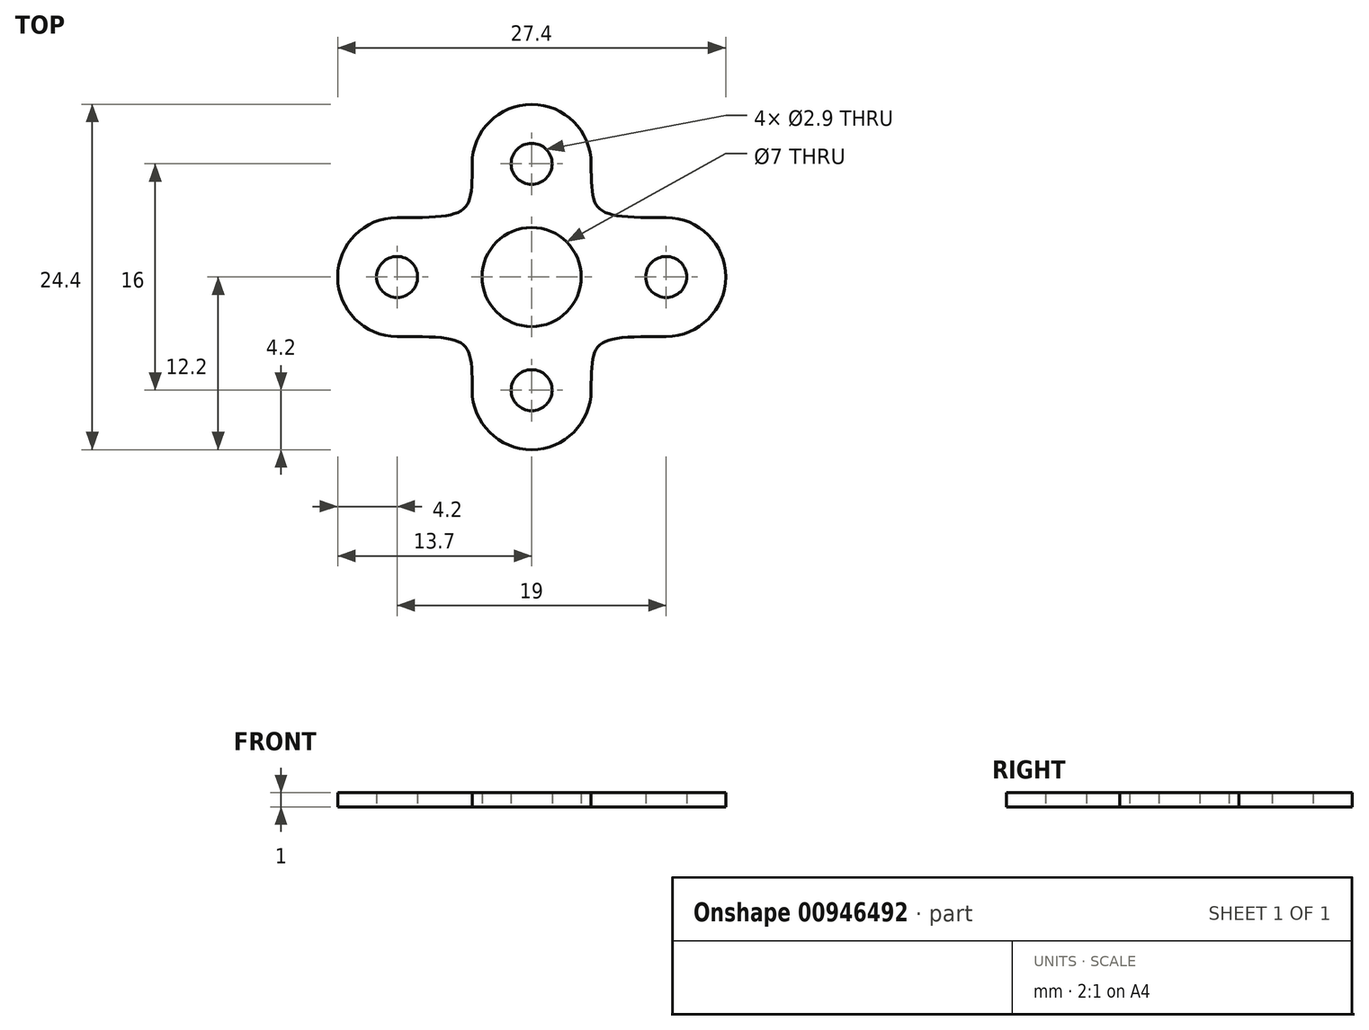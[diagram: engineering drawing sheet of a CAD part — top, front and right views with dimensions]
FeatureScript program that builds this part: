
annotation { "Feature Type Name" : "Feature", "Feature Type Description" : "" }
export const myFeature = defineFeature(function(context is Context, id is Id, definition is map)
    precondition{}
    {
        {
            assignVariable(context, id + "F0", {"name" : "thickness", "anyValue" : 1 * mm});
        }
        {
            var Q0;
            Q0=qCreatedBy(makeId("Top.planeOp"),FACE);
            var sketch = newSketch(context, id + "F1", { "sketchPlane" : qUnion([Q0])});
            skLineSegment(sketch, "E0", {"start": v(0, 8) * mm, "end": v(0, -8) * mm, "construction": true});
            skPoint(sketch, "E1", {"position": v(0, 0) * mm});
            skLineSegment(sketch, "E2", {"start": v(-9.5, 0) * mm, "end": v(9.5, 0) * mm, "construction": true});
            skCircle(sketch, "E3", {"center": v(0, 8) * mm, "radius": 1.45 * mm});
            skCircle(sketch, "E4", {"center": v(9.5, 0) * mm, "radius": 1.45 * mm});
            skCircle(sketch, "E5", {"center": v(0, -8) * mm, "radius": 1.45 * mm});
            skCircle(sketch, "E6", {"center": v(-9.5, 0) * mm, "radius": 1.45 * mm});
            skCircle(sketch, "E7", {"center": v(0, 0) * mm, "radius": 3.5 * mm});
            skCircle(sketch, "E8", {"center": v(0, 8) * mm, "radius": 4.2 * mm});
            skCircle(sketch, "E9", {"center": v(9.5, 0) * mm, "radius": 4.2 * mm});
            skCircle(sketch, "E10", {"center": v(0, -8) * mm, "radius": 4.2 * mm});
            skCircle(sketch, "E11", {"center": v(-9.5, 0) * mm, "radius": 4.2 * mm});
            skPoint(sketch, "E12", {"position": v(-9.5, 4.2) * mm});
            skPoint(sketch, "E13", {"position": v(-9.5, -4.2) * mm});
            skPoint(sketch, "E14", {"position": v(9.5, -4.2) * mm});
            skPoint(sketch, "E15", {"position": v(9.5, 4.2) * mm});
            skPoint(sketch, "E16", {"position": v(-4.2, 8) * mm});
            skPoint(sketch, "E17", {"position": v(4.2, 8) * mm});
            skPoint(sketch, "E18", {"position": v(4.2, -8) * mm});
            skPoint(sketch, "E19", {"position": v(-4.2, -8) * mm});
            skFitSpline(sketch, "E20", {"points": [v(-4.2, 8) * mm, v(-9.5, 4.2) * mm], "startDerivative": vector(0, -10.93) * mm, "endDerivative": vector(-15.53, 0) * mm});
            skFitSpline(sketch, "E21", {"points": [v(4.2, 8) * mm, v(9.5, 4.2) * mm], "startDerivative": vector(0, -10.93) * mm, "endDerivative": vector(15.53, 0) * mm});
            skFitSpline(sketch, "E22", {"points": [v(9.5, -4.2) * mm, v(4.2, -8) * mm], "startDerivative": vector(-15.53, 0) * mm, "endDerivative": vector(0, -10.93) * mm});
            skFitSpline(sketch, "E23", {"points": [v(-4.2, -8) * mm, v(-9.5, -4.2) * mm], "startDerivative": vector(0, 10.93) * mm, "endDerivative": vector(-15.53, 0) * mm});
            skLineSegment(sketch, "E24", {"start": v(-4.32, 4.2) * mm, "end": v(4.32, 4.2) * mm, "construction": true});
            skPoint(sketch, "E25", {"position": v(0, 4.2) * mm});
            skLineSegment(sketch, "E26", {"start": v(-4.32, -4.2) * mm, "end": v(4.32, -4.2) * mm, "construction": true});
            skPoint(sketch, "E27", {"position": v(0, -4.2) * mm});
            skLineSegment(sketch, "E28", {"start": v(-4.2, 4.36) * mm, "end": v(-4.2, -4.36) * mm, "construction": true});
            skLineSegment(sketch, "E29", {"start": v(4.2, 4.36) * mm, "end": v(4.2, -4.36) * mm, "construction": true});
            skPoint(sketch, "E30", {"position": v(-4.2, 0) * mm});
            skPoint(sketch, "E31", {"position": v(4.2, 0) * mm});
            skCircle(sketch, "E32", {"center": v(0, 8) * mm, "radius": 3 * mm});
            skCircle(sketch, "E33", {"center": v(9.5, 0) * mm, "radius": 3 * mm});
            skCircle(sketch, "E34", {"center": v(0, -8) * mm, "radius": 3 * mm});
            skCircle(sketch, "E35", {"center": v(-9.5, 0) * mm, "radius": 3 * mm});
            skSolve(sketch);
        }
        {
            var Q0;
            Q0=makeQuery(id+"F1.imprint","IMPRINT",FACE,{"disambiguationData":[TD([[makeQuery(id+"F1.imprint","IMPRINT",EDGE,{"derivedFrom":sQuery(id+"F1.wireOp",EDGE,"E7")}),-1.0]])]});
            var Q1;
            Q1=makeQuery(id+"F1.imprint","IMPRINT",FACE,{"disambiguationData":[TD([[makeQuery(id+"F1.imprint","IMPRINT",EDGE,{"derivedFrom":sQuery(id+"F1.wireOp",EDGE,"E3")}),-1.0]])]});
            var Q2;
            Q2=makeQuery(id+"F1.imprint","IMPRINT",FACE,{"disambiguationData":[TD([[makeQuery(id+"F1.imprint","IMPRINT",EDGE,{"derivedFrom":sQuery(id+"F1.wireOp",EDGE,"E6")}),-1.0]])]});
            var Q3;
            Q3=makeQuery(id+"F1.imprint","IMPRINT",FACE,{"disambiguationData":[TD([[makeQuery(id+"F1.imprint","IMPRINT",EDGE,{"derivedFrom":sQuery(id+"F1.wireOp",EDGE,"E5")}),-1.0]])]});
            var Q4;
            Q4=makeQuery(id+"F1.imprint","IMPRINT",FACE,{"disambiguationData":[TD([[makeQuery(id+"F1.imprint","IMPRINT",EDGE,{"derivedFrom":sQuery(id+"F1.wireOp",EDGE,"E4")}),-1.0]])]});
            var Q5;
            Q5=makeQuery(id+"F1.imprint","IMPRINT",FACE,{"disambiguationData":[TD([[makeQuery(id+"F1.imprint","IMPRINT",EDGE,{"derivedFrom":sQuery(id+"F1.wireOp",EDGE,"E35")}),-1.0]])]});
            var Q6;
            Q6=makeQuery(id+"F1.imprint","IMPRINT",FACE,{"disambiguationData":[TD([[makeQuery(id+"F1.imprint","IMPRINT",EDGE,{"derivedFrom":sQuery(id+"F1.wireOp",EDGE,"E34")}),-1.0]])]});
            var Q7;
            Q7=makeQuery(id+"F1.imprint","IMPRINT",FACE,{"disambiguationData":[TD([[makeQuery(id+"F1.imprint","IMPRINT",EDGE,{"derivedFrom":sQuery(id+"F1.wireOp",EDGE,"E33")}),-1.0]])]});
            var Q8;
            Q8=makeQuery(id+"F1.imprint","IMPRINT",FACE,{"disambiguationData":[TD([[makeQuery(id+"F1.imprint","IMPRINT",EDGE,{"derivedFrom":sQuery(id+"F1.wireOp",EDGE,"E32")}),-1.0]])]});
            extrude(context, id + "F2", {"entities" : qUnion([Q0, Q1, Q2, Q3, Q4, Q5, Q6, Q7, Q8]), "depth" : getVariable(context, 'thickness'), "offsetDistance" : 25 * mm});
        }
    });
